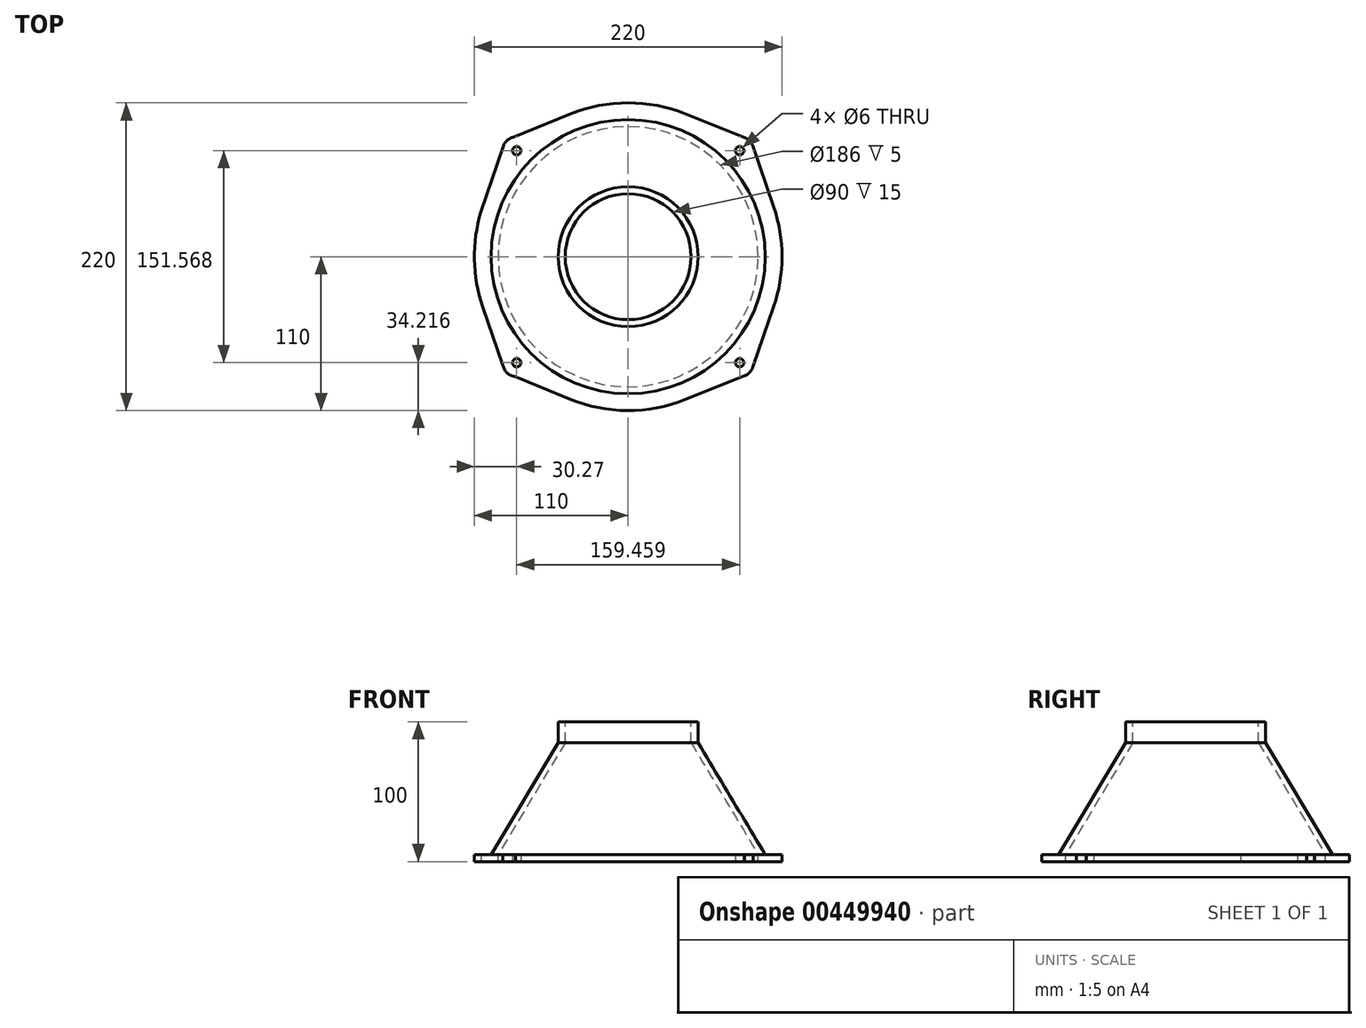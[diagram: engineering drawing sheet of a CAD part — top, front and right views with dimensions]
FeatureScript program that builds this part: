
annotation { "Feature Type Name" : "Feature", "Feature Type Description" : "" }
export const myFeature = defineFeature(function(context is Context, id is Id, definition is map)
    precondition{}
    {
        {
            var Q0;
            Q0=qCreatedBy(makeId("Top.planeOp"),FACE);
            var sketch = newSketch(context, id + "F0", { "sketchPlane" : qUnion([Q0])});
            skArc(sketch, "E0", {"start": v(-102.9, 38.86) * mm, "mid": v(-109.99, 1.53) * mm, "end": v(-103.95, -35.98) * mm});
            skCircle(sketch, "E1", {"center": v(79.73, 75.78) * mm, "radius": 3 * mm});
            skCircle(sketch, "E2", {"center": v(79.73, -75.78) * mm, "radius": 3 * mm});
            skCircle(sketch, "E3", {"center": v(-79.73, -75.78) * mm, "radius": 3 * mm});
            skCircle(sketch, "E4", {"center": v(-79.73, 75.78) * mm, "radius": 3 * mm});
            skCircle(sketch, "E5", {"center": v(0, 0) * mm, "radius": 95 * mm});
            skArc(sketch, "E6", {"start": v(89.35, 78.5) * mm, "mid": v(87.12, 82.52) * mm, "end": v(83.32, 85.12) * mm});
            skArc(sketch, "E7", {"start": v(82.96, -85.25) * mm, "mid": v(87.07, -82.58) * mm, "end": v(89.41, -78.28) * mm});
            skArc(sketch, "E8", {"start": v(-89.58, -77.48) * mm, "mid": v(-86.48, -83.17) * mm, "end": v(-80.54, -85.75) * mm});
            skArc(sketch, "E9", {"start": v(-82.35, 85.43) * mm, "mid": v(-86.73, 82.93) * mm, "end": v(-89.33, 78.6) * mm});
            skLineSegment(sketch, "E10", {"start": v(-89.33, 78.6) * mm, "end": v(-105.16, 32.26) * mm});
            skLineSegment(sketch, "E11", {"start": v(-82.35, 85.43) * mm, "end": v(-41.06, 102.05) * mm});
            skLineSegment(sketch, "E12", {"start": v(-89.58, -77.48) * mm, "end": v(-103.95, -35.98) * mm});
            skLineSegment(sketch, "E13", {"start": v(-80.54, -85.75) * mm, "end": v(-41.99, -101.67) * mm});
            skLineSegment(sketch, "E14", {"start": v(89, 79.55) * mm, "end": v(104.04, 35.71) * mm});
            skLineSegment(sketch, "E15", {"start": v(83.58, 85.01) * mm, "end": v(40.91, 102.1) * mm});
            skLineSegment(sketch, "E16", {"start": v(89.41, -78.28) * mm, "end": v(104.03, -35.75) * mm});
            skLineSegment(sketch, "E17", {"start": v(82.96, -85.25) * mm, "end": v(40.94, -102.1) * mm});
            skArc(sketch, "E18.trimOffspring", {"start": v(-41.99, -101.67) * mm, "mid": v(-0.56, -110) * mm, "end": v(40.94, -102.1) * mm});
            skArc(sketch, "E19.trimOffspring", {"start": v(104.03, -35.75) * mm, "mid": v(110, -0.02) * mm, "end": v(104.04, 35.71) * mm});
            skArc(sketch, "E20.trimOffspring", {"start": v(40.91, 102.1) * mm, "mid": v(-0.08, 110) * mm, "end": v(-41.06, 102.05) * mm});
            skPoint(sketch, "E21.bottom.end.orphan", {"position": v(-133.57, 126.96) * mm});
            skPoint(sketch, "E21.left.start.orphan", {"position": v(133.57, 126.96) * mm});
            skPoint(sketch, "E21.top.end.orphan", {"position": v(-133.57, -126.96) * mm});
            skPoint(sketch, "E21.top.start.orphan", {"position": v(133.57, -126.96) * mm});
            skSolve(sketch);
        }
        {
            var Q0;
            Q0=qCreatedBy(makeId("Front.planeOp"),FACE);
            var sketch = newSketch(context, id + "F1", { "sketchPlane" : qUnion([Q0])});
            skLineSegment(sketch, "E22", {"start": v(0, 100) * mm, "end": v(0, 0) * mm});
            skLineSegment(sketch, "E23", {"start": v(-98, 0) * mm, "end": v(-93, 0) * mm});
            skLineSegment(sketch, "E24", {"start": v(-50, 100) * mm, "end": v(-45, 100) * mm});
            skLineSegment(sketch, "E25", {"start": v(-98, 0) * mm, "end": v(-98, 5) * mm});
            skLineSegment(sketch, "E26", {"start": v(-93, 5) * mm, "end": v(-93, 0) * mm});
            skLineSegment(sketch, "E27", {"start": v(-45, 85) * mm, "end": v(-45, 100) * mm});
            skLineSegment(sketch, "E28", {"start": v(-50, 85) * mm, "end": v(-50, 100) * mm});
            skLineSegment(sketch, "E29", {"start": v(-98, 5) * mm, "end": v(-50, 85) * mm});
            skLineSegment(sketch, "E30", {"start": v(-45, 85) * mm, "end": v(-93, 5) * mm});
            skPoint(sketch, "E31.end.orphan", {"position": v(93, 0) * mm});
            skPoint(sketch, "E31.start.orphan", {"position": v(98, 0) * mm});
            skPoint(sketch, "E32.start.orphan", {"position": v(50, 100) * mm});
            skPoint(sketch, "E33.start.orphan", {"position": v(45, 100) * mm});
            skSolve(sketch);
        }
        {
            var Q0;
            Q0=makeQuery(id+"F1.imprint","IMPRINT",FACE,{"disambiguationData":[TD([[makeQuery(id+"F1.imprint","IMPRINT",EDGE,{"derivedFrom":sQuery(id+"F1.wireOp",EDGE,"E23")}),1.0]])]});
            var Q1;
            Q1=sQuery(id+"F1.wireOp",EDGE,"E22");
            revolve(context, id + "F2", {"entities" : qUnion([Q0]), "axis" : qUnion([Q1]), "revolveType" : RevolveType.FULL});
        }
        {
            var Q0;
            Q0=makeQuery(id+"F0.imprint","IMPRINT",FACE,{"disambiguationData":[TD([[makeQuery(id+"F0.imprint","IMPRINT",EDGE,{"derivedFrom":sQuery(id+"F0.wireOp",EDGE,"E1")}),-1.0]])]});
            extrude(context, id + "F3", {"entities" : qUnion([Q0]), "operationType" : NewBodyOperationType.ADD, "depth" : 5 * mm});
        }
    });
